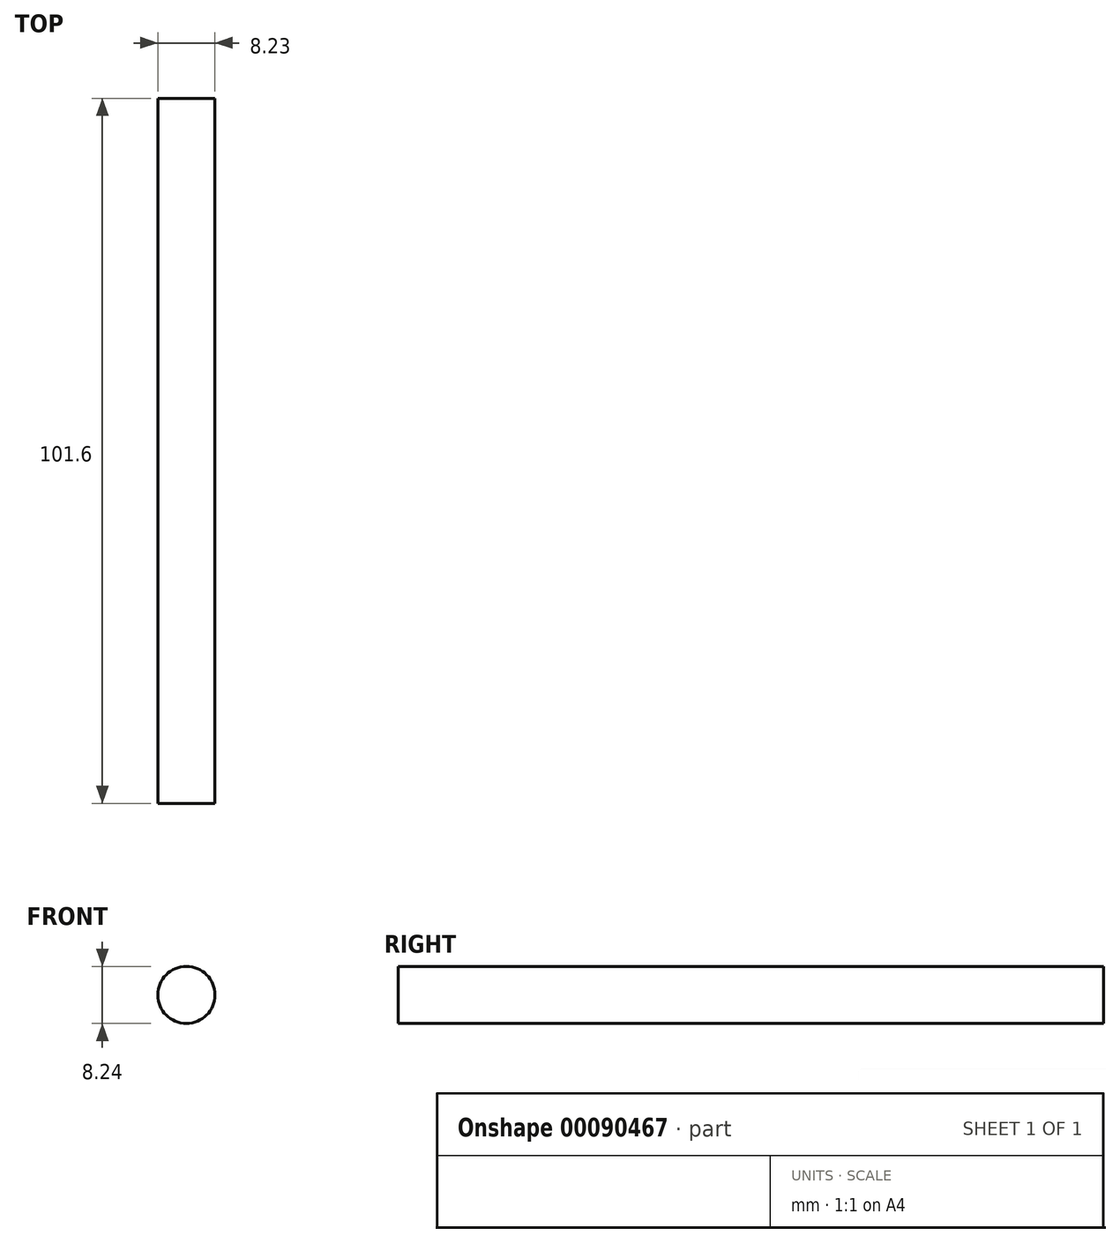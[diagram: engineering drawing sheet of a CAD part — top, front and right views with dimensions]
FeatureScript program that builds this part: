
annotation { "Feature Type Name" : "Feature", "Feature Type Description" : "" }
export const myFeature = defineFeature(function(context is Context, id is Id, definition is map)
    precondition{}
    {
        {
            var Q0;
            Q0=qCreatedBy(makeId("Front.planeOp"),FACE);
            var sketch = newSketch(context, id + "F0", { "sketchPlane" : qUnion([Q0])});
            skCircle(sketch, "E0", {"center": v(-26.25, 6.17) * mm, "radius": 4.12 * mm});
            skSolve(sketch);
        }
        {
            var Q0;
            Q0=makeQuery(id+"F0.imprint","IMPRINT",FACE,{"disambiguationData":[TD([[makeQuery(id+"F0.imprint","IMPRINT",EDGE,{"derivedFrom":sQuery(id+"F0.wireOp",EDGE,"E0")}),1.0]])]});
            extrude(context, id + "F1", {"entities" : qUnion([Q0]), "endBound" : BoundingType.SYMMETRIC, "depth" : 101.6 * mm});
        }
    });
